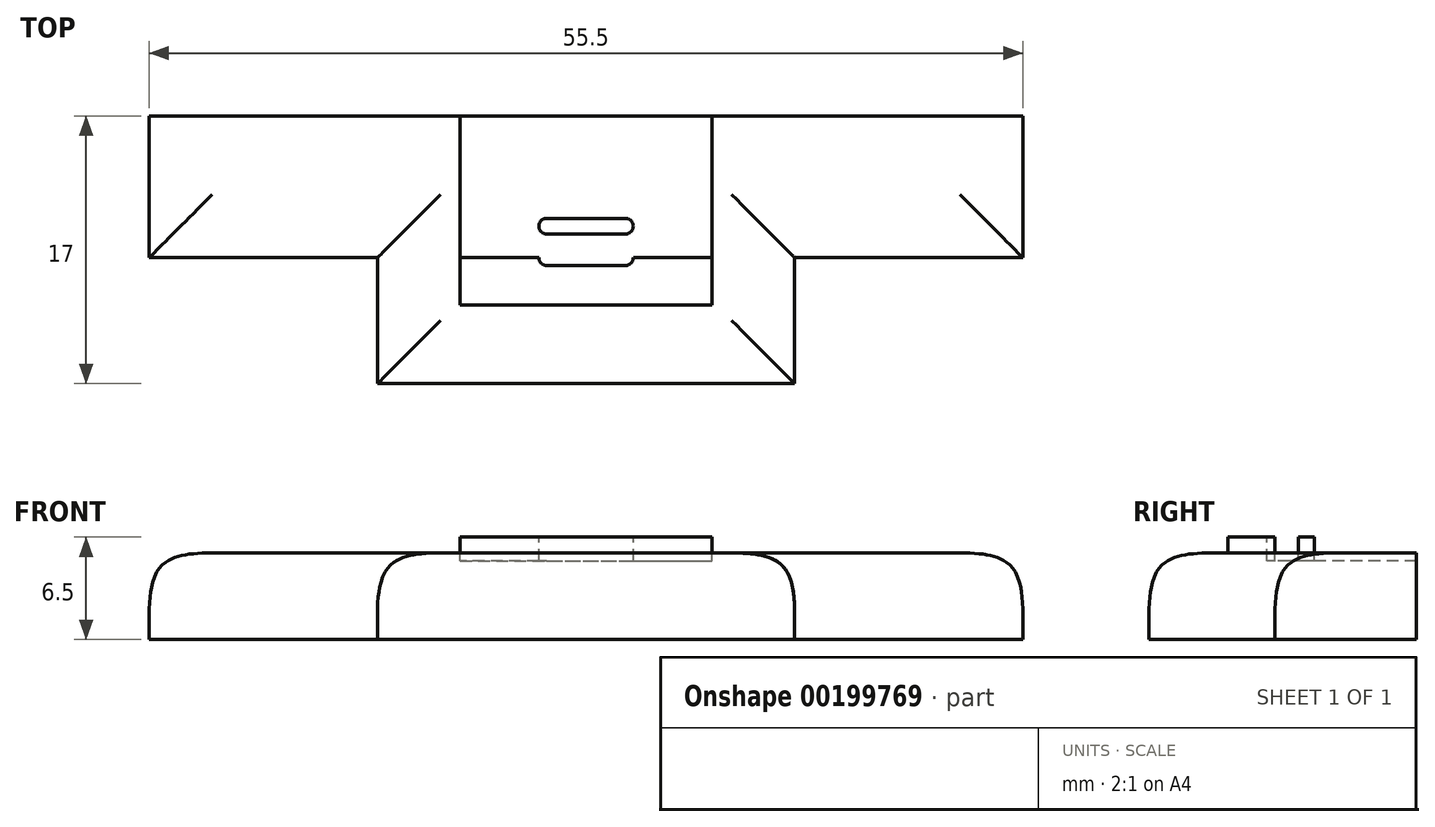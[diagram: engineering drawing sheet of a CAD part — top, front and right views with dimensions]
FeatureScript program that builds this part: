
annotation { "Feature Type Name" : "Feature", "Feature Type Description" : "" }
export const myFeature = defineFeature(function(context is Context, id is Id, definition is map)
    precondition{}
    {
        {
            var Q0;
            Q0=qCreatedBy(makeId("Top.planeOp"),FACE);
            var sketch = newSketch(context, id + "F0", { "sketchPlane" : qUnion([Q0])});
            skLineSegment(sketch, "E0", {"start": v(0, 0) * mm, "end": v(55.5, 0) * mm});
            skLineSegment(sketch, "E1", {"start": v(55.5, 0) * mm, "end": v(55.5, -9) * mm});
            skLineSegment(sketch, "E2", {"start": v(55.5, -9) * mm, "end": v(41, -9) * mm});
            skLineSegment(sketch, "E3", {"start": v(41, -9) * mm, "end": v(41, -17) * mm});
            skLineSegment(sketch, "E4", {"start": v(41, -17) * mm, "end": v(14.5, -17) * mm});
            skLineSegment(sketch, "E5", {"start": v(14.5, -17) * mm, "end": v(14.5, -9) * mm});
            skLineSegment(sketch, "E6", {"start": v(14.5, -9) * mm, "end": v(0, -9) * mm});
            skLineSegment(sketch, "E7", {"start": v(0, -9) * mm, "end": v(0, 0) * mm});
            skSolve(sketch);
        }
        {
            var Q0;
            Q0=makeQuery(id+"F0.imprint","IMPRINT",FACE,{"disambiguationData":[TD([[makeQuery(id+"F0.imprint","IMPRINT",EDGE,{"derivedFrom":sQuery(id+"F0.wireOp",EDGE,"E0")}),-1.0]])]});
            extrude(context, id + "F1", {"entities" : qUnion([Q0]), "depth" : 5.5 * mm});
        }
        {
            var Q0;
            Q0=makeQuery(id+"F1.opExtrude","CAP_EDGE",EDGE,{"disambiguationData":[OSD([sQuery(id+"F0.wireOp",EDGE,"E6")])],"isStart":false});
            var Q1;
            Q1=makeQuery(id+"F1.opExtrude","CAP_EDGE",EDGE,{"disambiguationData":[OSD([sQuery(id+"F0.wireOp",EDGE,"E7")])],"isStart":false});
            var Q2;
            Q2=makeQuery(id+"F1.opExtrude","CAP_EDGE",EDGE,{"disambiguationData":[OSD([sQuery(id+"F0.wireOp",EDGE,"E4")])],"isStart":false});
            var Q3;
            Q3=makeQuery(id+"F1.opExtrude","CAP_EDGE",EDGE,{"disambiguationData":[OSD([sQuery(id+"F0.wireOp",EDGE,"E3")])],"isStart":false});
            var Q4;
            Q4=makeQuery(id+"F1.opExtrude","CAP_EDGE",EDGE,{"disambiguationData":[OSD([sQuery(id+"F0.wireOp",EDGE,"E5")])],"isStart":false});
            var Q5;
            Q5=makeQuery(id+"F1.opExtrude","CAP_EDGE",EDGE,{"disambiguationData":[OSD([sQuery(id+"F0.wireOp",EDGE,"E2")])],"isStart":false});
            var Q6;
            Q6=makeQuery(id+"F1.opExtrude","CAP_EDGE",EDGE,{"disambiguationData":[OSD([sQuery(id+"F0.wireOp",EDGE,"E1")])],"isStart":false});
            fillet(context, id + "F2", {"entities" : qUnion([Q0, Q1, Q2, Q3, Q4, Q5, Q6]), "radius" : 4 * mm, "tangentPropagation" : true, "rho" : 0.6, "crossSection" : FilletCrossSection.CONIC, "allowEdgeOverflow" : false});
        }
        {
            var Q0;
            Q0=makeQuery(id+"F1.opExtrude","CAP_FACE",FACE,{"disambiguationData":[OSD([sQuery(id+"F0.wireOp",EDGE,"E0"),sQuery(id+"F0.wireOp",EDGE,"E1"),sQuery(id+"F0.wireOp",EDGE,"E2"),sQuery(id+"F0.wireOp",EDGE,"E3"),sQuery(id+"F0.wireOp",EDGE,"E4"),sQuery(id+"F0.wireOp",EDGE,"E5"),sQuery(id+"F0.wireOp",EDGE,"E6"),sQuery(id+"F0.wireOp",EDGE,"E7")])],"isStart":false});
            var sketch = newSketch(context, id + "F3", { "sketchPlane" : qUnion([Q0])});
            skLineSegment(sketch, "E8.bottom", {"start": v(19.75, 0) * mm, "end": v(35.75, 0) * mm});
            skLineSegment(sketch, "E8.top", {"start": v(19.75, -12) * mm, "end": v(35.75, -12) * mm});
            skLineSegment(sketch, "E8.left", {"start": v(19.75, 0) * mm, "end": v(19.75, -12) * mm});
            skLineSegment(sketch, "E8.right", {"start": v(35.75, 0) * mm, "end": v(35.75, -12) * mm});
            skLineSegment(sketch, "E9", {"start": v(0, 0) * mm, "end": v(19.75, 0) * mm});
            skPoint(sketch, "E10.0", {"position": v(55.5, 0) * mm});
            skLineSegment(sketch, "E11", {"start": v(55.5, 0) * mm, "end": v(35.75, 0) * mm});
            skSolve(sketch);
        }
        {
            var Q0;
            Q0=makeQuery(id+"F3.imprint","IMPRINT",FACE,{"disambiguationData":[TD([[makeQuery(id+"F3.imprint","IMPRINT",EDGE,{"derivedFrom":sQuery(id+"F3.wireOp",EDGE,"E8.bottom")}),-1.0]])]});
            extrude(context, id + "F4", {"entities" : qUnion([Q0]), "operationType" : NewBodyOperationType.ADD, "depth" : 1 * mm});
        }
        {
            var Q0;
            Q0=makeQuery(id+"F4.opExtrude","CAP_FACE",FACE,{"disambiguationData":[OSD([sQuery(id+"F3.wireOp",EDGE,"E8.bottom"),sQuery(id+"F3.wireOp",EDGE,"E8.top"),sQuery(id+"F3.wireOp",EDGE,"E8.left"),sQuery(id+"F3.wireOp",EDGE,"E8.right")])],"isStart":false});
            var sketch = newSketch(context, id + "F5", { "sketchPlane" : qUnion([Q0])});
            skLineSegment(sketch, "E12", {"start": v(25.25, -9) * mm, "end": v(30.25, -9) * mm});
            skLineSegment(sketch, "E13", {"start": v(25.25, -7) * mm, "end": v(30.25, -7) * mm});
            skLineSegment(sketch, "E14", {"start": v(25.25, -9) * mm, "end": v(19.75, -9) * mm});
            skLineSegment(sketch, "E15", {"start": v(30.25, -9) * mm, "end": v(35.75, -9) * mm});
            skArc(sketch, "E16.0.startCap", {"start": v(25.25, -7.5) * mm, "mid": v(24.75, -7) * mm, "end": v(25.25, -6.5) * mm});
            skArc(sketch, "E16.0.endCap", {"start": v(30.25, -6.5) * mm, "mid": v(30.75, -7) * mm, "end": v(30.25, -7.5) * mm});
            skLineSegment(sketch, "E16.0.left", {"start": v(25.25, -6.5) * mm, "end": v(30.25, -6.5) * mm});
            skLineSegment(sketch, "E16.0.right", {"start": v(25.25, -7.5) * mm, "end": v(30.25, -7.5) * mm});
            skArc(sketch, "E16.1.startCap", {"start": v(25.25, -9.5) * mm, "mid": v(24.75, -9) * mm, "end": v(25.25, -8.5) * mm});
            skArc(sketch, "E16.1.endCap", {"start": v(30.25, -8.5) * mm, "mid": v(30.75, -9) * mm, "end": v(30.25, -9.5) * mm});
            skLineSegment(sketch, "E16.1.left", {"start": v(25.25, -8.5) * mm, "end": v(30.25, -8.5) * mm});
            skLineSegment(sketch, "E16.1.right", {"start": v(25.25, -9.5) * mm, "end": v(30.25, -9.5) * mm});
            skSolve(sketch);
        }
        {
            var Q0;
            Q0=makeQuery(id+"F5.imprint","IMPRINT",FACE,{"disambiguationData":[TD([[makeQuery(id+"F5.imprint","IMPRINT",EDGE,{"derivedFrom":sQuery(id+"F5.wireOp",EDGE,"E16.0.startCap")}),-1.0]])]});
            var Q1;
            {var subQ7=sQuery(id+"F5.wireOp",EDGE,"E12");Q1=makeQuery(id+"F5.imprint","IMPRINT",FACE,{"disambiguationData":[TD([[makeQuery(id+"F5.imprint","IMPRINT",EDGE,{"derivedFrom":subQ7}),-1.0]])]});}
            var Q2;
            {var subQ1=sQuery(id+"F5.wireOp",EDGE,"E12");Q2=makeQuery(id+"F5.imprint","IMPRINT",FACE,{"disambiguationData":[TD([[makeQuery(id+"F5.imprint","IMPRINT",EDGE,{"derivedFrom":subQ1}),1.0]])]});}
            extrude(context, id + "F6", {"entities" : qUnion([Q0, Q1, Q2]), "operationType" : NewBodyOperationType.REMOVE, "oppositeDirection" : true, "depth" : 1.5 * mm});
        }
    });
